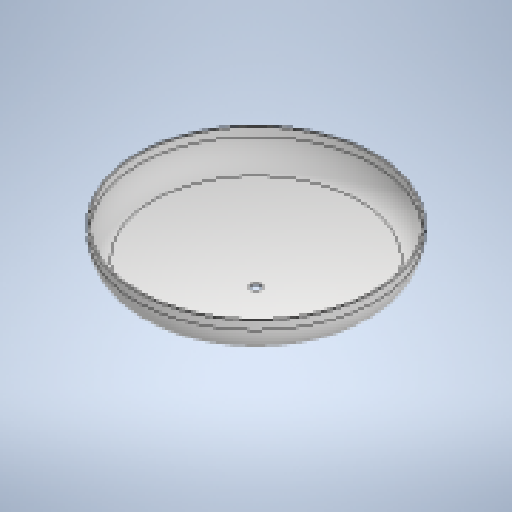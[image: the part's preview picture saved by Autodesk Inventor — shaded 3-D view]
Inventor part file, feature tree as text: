
AUTODESK INVENTOR PART (.ipt)
format: ipt  version: 2025.3 (Build 293356030, 356C)  size: 189,952 bytes
history: native  units: mm
features: sketch x2, revolve x1, extrude x1
ambient origin geometry x8: Origin, YZ Plane, XZ Plane, XY Plane, X Axis, Y Axis, Z Axis, Center Point
bodies: Solid1 (feature_tree)
feature tree (4):
  revolve  "Revolution1"  [1 undecoded]
  extrude  "Extrusion1"  Depth=841.666667mm
  sketch  "Sketch1"  dims[d0=100.0mm d1=30.0mm]
  sketch  "Sketch2"  dims[d3=841.666667mm d6=6.0mm d7=90.0deg d8=33.5mm d9=0.0mm d10=0.0mm d11=838.0mm d12=205.0mm]
note: 1 required parameter value undecoded (feature->parameter linkage not recoverable at this tier; creation-order binding heuristic only, values carry confidence <= 0.55)
